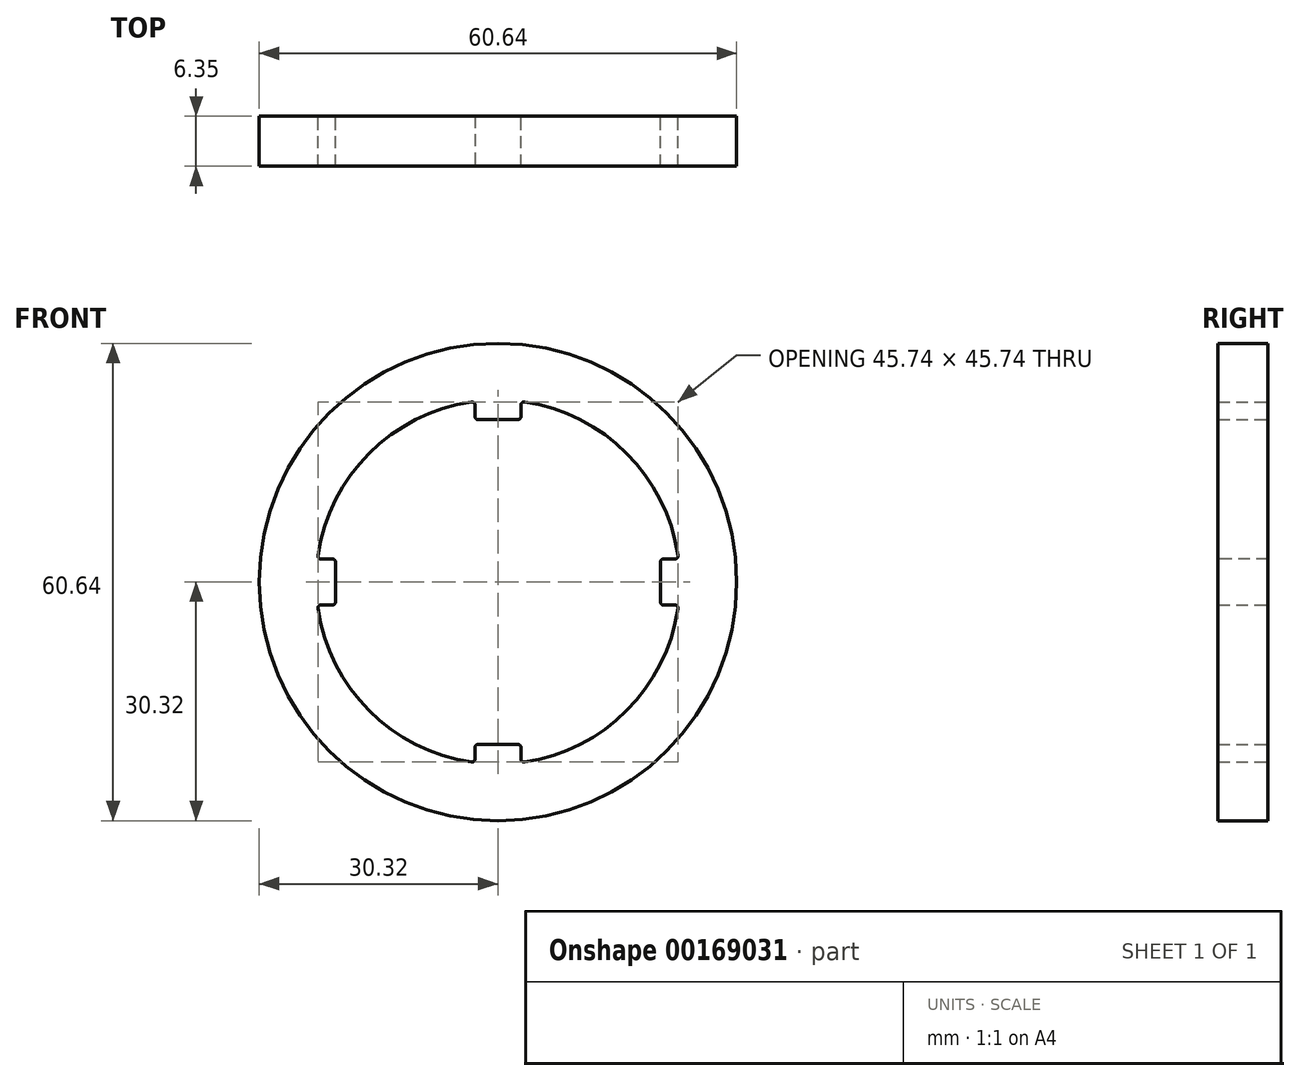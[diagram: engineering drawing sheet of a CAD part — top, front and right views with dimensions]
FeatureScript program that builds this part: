
annotation { "Feature Type Name" : "Feature", "Feature Type Description" : "" }
export const myFeature = defineFeature(function(context is Context, id is Id, definition is map)
    precondition{}
    {
        {
            var Q0;
            Q0=qCreatedBy(makeId("Front.planeOp"),FACE);
            var sketch = newSketch(context, id + "F0", { "sketchPlane" : qUnion([Q0])});
            skCircle(sketch, "E0", {"center": v(0, 0) * mm, "radius": 30.32 * mm});
            skArc(sketch, "E1", {"start": v(-22.93, -2.92) * mm, "mid": v(-16.34, -16.34) * mm, "end": v(-2.92, -22.93) * mm});
            skLineSegment(sketch, "E2", {"start": v(0, 30.32) * mm, "end": v(0, -30.32) * mm, "construction": true});
            skLineSegment(sketch, "E3", {"start": v(30.32, 0) * mm, "end": v(-30.32, 0) * mm, "construction": true});
            skLineSegment(sketch, "E4.top", {"start": v(-2.92, 20.64) * mm, "end": v(2.92, 20.64) * mm});
            skLineSegment(sketch, "E4.left", {"start": v(-2.92, 22.93) * mm, "end": v(-2.92, 20.64) * mm});
            skLineSegment(sketch, "E4.right", {"start": v(2.92, 22.93) * mm, "end": v(2.92, 20.64) * mm});
            skLineSegment(sketch, "E5.bottom", {"start": v(22.93, 2.92) * mm, "end": v(20.64, 2.92) * mm});
            skLineSegment(sketch, "E5.top", {"start": v(22.93, -2.92) * mm, "end": v(20.64, -2.92) * mm});
            skLineSegment(sketch, "E5.right", {"start": v(20.64, 2.92) * mm, "end": v(20.64, -2.92) * mm});
            skLineSegment(sketch, "E6.top", {"start": v(2.92, -20.64) * mm, "end": v(-2.92, -20.64) * mm});
            skLineSegment(sketch, "E6.left", {"start": v(2.92, -22.93) * mm, "end": v(2.92, -20.64) * mm});
            skLineSegment(sketch, "E6.right", {"start": v(-2.92, -22.93) * mm, "end": v(-2.92, -20.64) * mm});
            skLineSegment(sketch, "E7.bottom", {"start": v(-22.93, 2.92) * mm, "end": v(-20.64, 2.92) * mm});
            skLineSegment(sketch, "E7.top", {"start": v(-22.93, -2.92) * mm, "end": v(-20.64, -2.92) * mm});
            skLineSegment(sketch, "E7.right", {"start": v(-20.64, 2.92) * mm, "end": v(-20.64, -2.92) * mm});
            skArc(sketch, "E8.trimOffspring", {"start": v(2.92, -22.93) * mm, "mid": v(16.34, -16.34) * mm, "end": v(22.93, -2.92) * mm});
            skPoint(sketch, "E6.bottom.start.orphan", {"position": v(2.92, -25.4) * mm});
            skArc(sketch, "E9.trimOffspring", {"start": v(22.93, 2.92) * mm, "mid": v(16.34, 16.34) * mm, "end": v(2.92, 22.93) * mm});
            skArc(sketch, "E10.trimOffspring", {"start": v(-2.92, 22.93) * mm, "mid": v(-16.34, 16.34) * mm, "end": v(-22.93, 2.92) * mm});
            skSolve(sketch);
        }
        {
            var Q0;
            Q0=makeQuery(id+"F0.imprint","IMPRINT",FACE,{"disambiguationData":[TD([[makeQuery(id+"F0.imprint","IMPRINT",EDGE,{"derivedFrom":sQuery(id+"F0.wireOp",EDGE,"E0")}),1.0]])]});
            extrude(context, id + "F1", {"entities" : qUnion([Q0]), "depth" : 6.35 * mm});
        }
        {
            var Q0;
            Q0=makeQuery(id+"F1.opExtrude","SWEPT_EDGE",EDGE,{"disambiguationData":[OSD([sQuery(id+"F0.wireOp",EDGE,"E4.top"),sQuery(id+"F0.wireOp",EDGE,"E4.left")])]});
            var Q1;
            Q1=makeQuery(id+"F1.opExtrude","SWEPT_EDGE",EDGE,{"disambiguationData":[OSD([sQuery(id+"F0.wireOp",EDGE,"E4.left"),sQuery(id+"F0.wireOp",EDGE,"E10.trimOffspring")])]});
            var Q2;
            Q2=makeQuery(id+"F1.opExtrude","SWEPT_EDGE",EDGE,{"disambiguationData":[OSD([sQuery(id+"F0.wireOp",EDGE,"E4.top"),sQuery(id+"F0.wireOp",EDGE,"E4.right")])]});
            var Q3;
            Q3=makeQuery(id+"F1.opExtrude","SWEPT_EDGE",EDGE,{"disambiguationData":[OSD([sQuery(id+"F0.wireOp",EDGE,"E7.top"),sQuery(id+"F0.wireOp",EDGE,"E7.right")])]});
            var Q4;
            Q4=makeQuery(id+"F1.opExtrude","SWEPT_EDGE",EDGE,{"disambiguationData":[OSD([sQuery(id+"F0.wireOp",EDGE,"E5.top"),sQuery(id+"F0.wireOp",EDGE,"E8.trimOffspring")])]});
            var Q5;
            Q5=makeQuery(id+"F1.opExtrude","SWEPT_EDGE",EDGE,{"disambiguationData":[OSD([sQuery(id+"F0.wireOp",EDGE,"E5.top"),sQuery(id+"F0.wireOp",EDGE,"E5.right")])]});
            var Q6;
            Q6=makeQuery(id+"F1.opExtrude","SWEPT_EDGE",EDGE,{"disambiguationData":[OSD([sQuery(id+"F0.wireOp",EDGE,"E5.bottom"),sQuery(id+"F0.wireOp",EDGE,"E5.right")])]});
            var Q7;
            Q7=makeQuery(id+"F1.opExtrude","SWEPT_EDGE",EDGE,{"disambiguationData":[OSD([sQuery(id+"F0.wireOp",EDGE,"E6.top"),sQuery(id+"F0.wireOp",EDGE,"E6.right")])]});
            var Q8;
            Q8=makeQuery(id+"F1.opExtrude","SWEPT_EDGE",EDGE,{"disambiguationData":[OSD([sQuery(id+"F0.wireOp",EDGE,"E6.top"),sQuery(id+"F0.wireOp",EDGE,"E6.left")])]});
            var Q9;
            Q9=makeQuery(id+"F1.opExtrude","SWEPT_EDGE",EDGE,{"disambiguationData":[OSD([sQuery(id+"F0.wireOp",EDGE,"E1"),sQuery(id+"F0.wireOp",EDGE,"E6.right")])]});
            var Q10;
            Q10=makeQuery(id+"F1.opExtrude","SWEPT_EDGE",EDGE,{"disambiguationData":[OSD([sQuery(id+"F0.wireOp",EDGE,"E7.bottom"),sQuery(id+"F0.wireOp",EDGE,"E7.right")])]});
            var Q11;
            Q11=makeQuery(id+"F1.opExtrude","SWEPT_EDGE",EDGE,{"disambiguationData":[OSD([sQuery(id+"F0.wireOp",EDGE,"E5.bottom"),sQuery(id+"F0.wireOp",EDGE,"E9.trimOffspring")])]});
            var Q12;
            Q12=makeQuery(id+"F1.opExtrude","SWEPT_EDGE",EDGE,{"disambiguationData":[OSD([sQuery(id+"F0.wireOp",EDGE,"E4.right"),sQuery(id+"F0.wireOp",EDGE,"E9.trimOffspring")])]});
            var Q13;
            Q13=makeQuery(id+"F1.opExtrude","SWEPT_EDGE",EDGE,{"disambiguationData":[OSD([sQuery(id+"F0.wireOp",EDGE,"E1"),sQuery(id+"F0.wireOp",EDGE,"E7.top")])]});
            var Q14;
            Q14=makeQuery(id+"F1.opExtrude","SWEPT_EDGE",EDGE,{"disambiguationData":[OSD([sQuery(id+"F0.wireOp",EDGE,"E6.left"),sQuery(id+"F0.wireOp",EDGE,"E8.trimOffspring")])]});
            var Q15;
            Q15=makeQuery(id+"F1.opExtrude","SWEPT_EDGE",EDGE,{"disambiguationData":[OSD([sQuery(id+"F0.wireOp",EDGE,"E7.bottom"),sQuery(id+"F0.wireOp",EDGE,"E10.trimOffspring")])]});
            fillet(context, id + "F2", {"entities" : qUnion([Q0, Q1, Q2, Q3, Q4, Q5, Q6, Q7, Q8, Q9, Q10, Q11, Q12, Q13, Q14, Q15]), "radius" : 0.38 * mm, "tangentPropagation" : true, "allowEdgeOverflow" : false});
        }
    });
